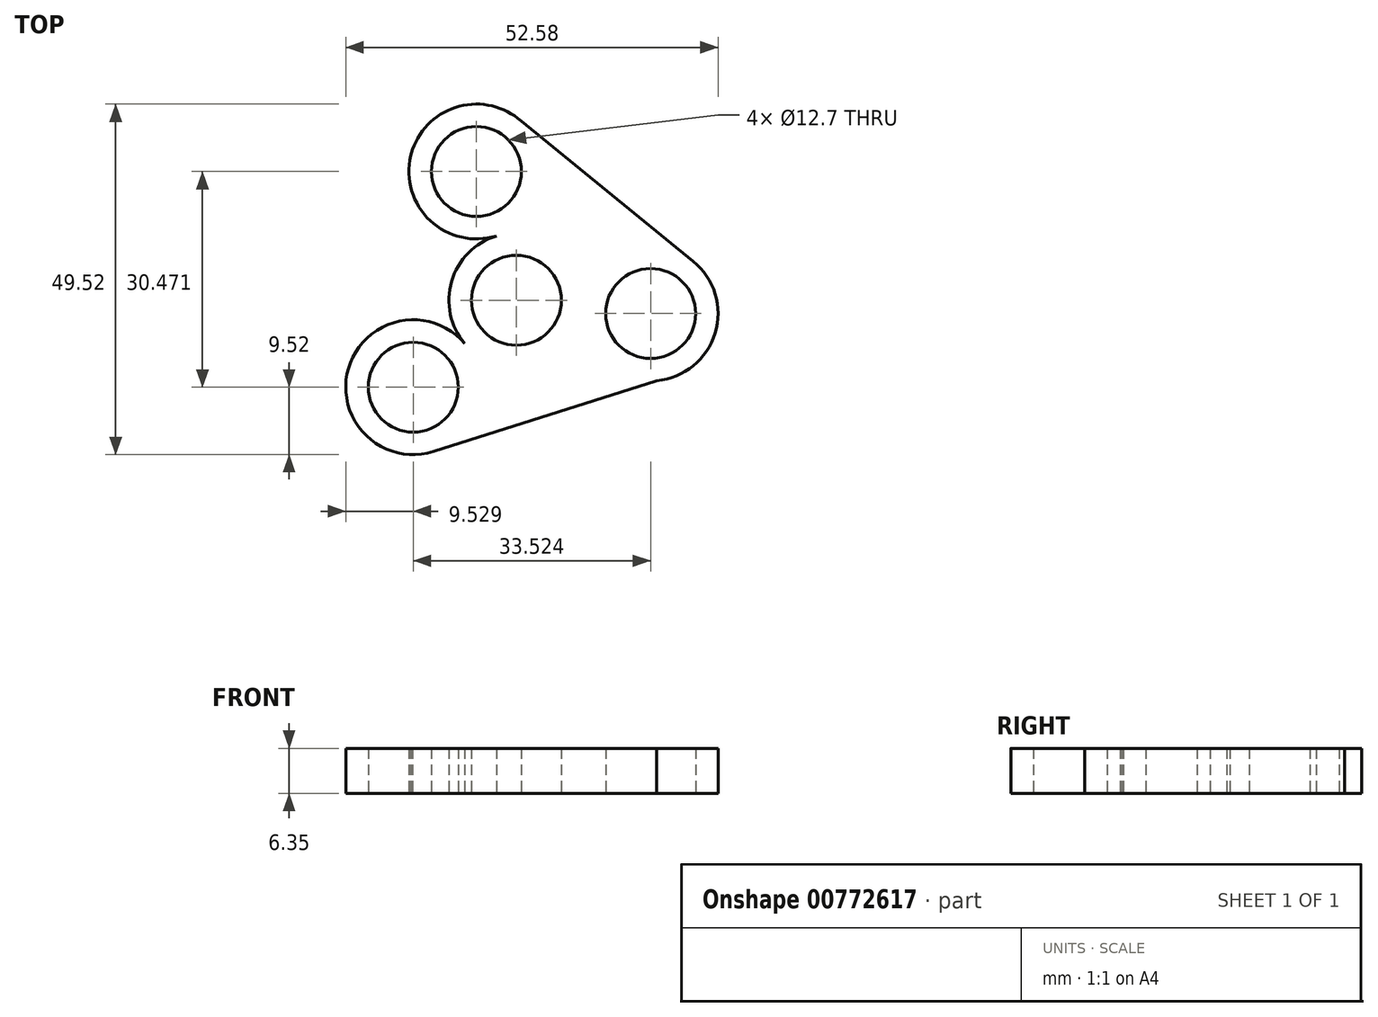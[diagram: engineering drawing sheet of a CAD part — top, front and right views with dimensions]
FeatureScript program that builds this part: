
annotation { "Feature Type Name" : "Feature", "Feature Type Description" : "" }
export const myFeature = defineFeature(function(context is Context, id is Id, definition is map)
    precondition{}
    {
        {
            var Q0;
            Q0=qCreatedBy(makeId("Top.planeOp"),FACE);
            var sketch = newSketch(context, id + "F0", { "sketchPlane" : qUnion([Q0])});
            skCircle(sketch, "E0", {"center": v(-56, 50.78) * mm, "radius": 9.53 * mm});
            skCircle(sketch, "E1", {"center": v(-31.4, 30.71) * mm, "radius": 9.53 * mm});
            skCircle(sketch, "E2", {"center": v(-50.36, 32.59) * mm, "radius": 9.53 * mm});
            skCircle(sketch, "E3", {"center": v(-64.92, 20.31) * mm, "radius": 9.53 * mm});
            skLineSegment(sketch, "E4", {"start": v(-49.69, 57.91) * mm, "end": v(-25.38, 38.1) * mm});
            skLineSegment(sketch, "E5", {"start": v(-30.53, 21.23) * mm, "end": v(-62.04, 11.23) * mm});
            skLineSegment(sketch, "E6", {"start": v(-65, 53.91) * mm, "end": v(-74.06, 22.99) * mm});
            skCircle(sketch, "E7", {"center": v(-64.92, 20.31) * mm, "radius": 6.35 * mm});
            skCircle(sketch, "E8", {"center": v(-50.36, 32.59) * mm, "radius": 6.35 * mm});
            skCircle(sketch, "E9", {"center": v(-56, 50.78) * mm, "radius": 6.35 * mm});
            skCircle(sketch, "E10", {"center": v(-31.4, 30.71) * mm, "radius": 6.35 * mm});
            skSolve(sketch);
        }
        {
            var Q0;
            {var subQ0=sQuery(id+"F0.wireOp",EDGE,"E0");var subQ1=makeQuery(id+"F0.imprint","INTERSECT",VERTEX,{"derivedFrom":[subQ0,sQuery(id+"F0.wireOp",EDGE,"E4")]});Q0=makeQuery(id+"F0.imprint","IMPRINT",FACE,{"disambiguationData":[TD([[makeQuery(id+"F0.imprint","IMPRINT",EDGE,{"disambiguationData":[TD([[subQ1,-1.0]])],"derivedFrom":subQ0}),1.0]])]});}
            var Q1;
            {var subQ0=sQuery(id+"F0.wireOp",EDGE,"E6");var subQ1=sQuery(id+"F0.wireOp",EDGE,"E0");var subQ2=makeQuery(id+"F0.imprint","INTERSECT",VERTEX,{"disambiguationData":[OD(0.0)],"derivedFrom":[subQ1,subQ0]});Q1=makeQuery(id+"F0.imprint","IMPRINT",FACE,{"disambiguationData":[TD([[makeQuery(id+"F0.imprint","IMPRINT",EDGE,{"disambiguationData":[TD([[subQ2,-1.0]])],"derivedFrom":subQ1}),1.0]])]});}
            var Q2;
            {var subQ0=sQuery(id+"F0.wireOp",EDGE,"E1");var subQ1=makeQuery(id+"F0.imprint","INTERSECT",VERTEX,{"derivedFrom":[subQ0,sQuery(id+"F0.wireOp",EDGE,"E4")]});Q2=makeQuery(id+"F0.imprint","IMPRINT",FACE,{"disambiguationData":[TD([[makeQuery(id+"F0.imprint","IMPRINT",EDGE,{"disambiguationData":[TD([[subQ1,-1.0]])],"derivedFrom":subQ0}),1.0]])]});}
            var Q3;
            {var subQ0=sQuery(id+"F0.wireOp",EDGE,"E3");var subQ1=makeQuery(id+"F0.imprint","INTERSECT",VERTEX,{"derivedFrom":[subQ0,sQuery(id+"F0.wireOp",EDGE,"E6")]});Q3=makeQuery(id+"F0.imprint","IMPRINT",FACE,{"disambiguationData":[TD([[makeQuery(id+"F0.imprint","IMPRINT",EDGE,{"disambiguationData":[TD([[subQ1,1.0]])],"derivedFrom":subQ0}),1.0]])]});}
            var Q4;
            {var subQ0=sQuery(id+"F0.wireOp",EDGE,"E6");var subQ1=sQuery(id+"F0.wireOp",EDGE,"E0");var subQ2=makeQuery(id+"F0.imprint","INTERSECT",VERTEX,{"disambiguationData":[OD(1.0)],"derivedFrom":[subQ1,subQ0]});Q4=makeQuery(id+"F0.imprint","IMPRINT",FACE,{"disambiguationData":[TD([[makeQuery(id+"F0.imprint","IMPRINT",EDGE,{"disambiguationData":[TD([[subQ2,-1.0]])],"derivedFrom":subQ1}),-1.0]])]});}
            var Q5;
            {var subQ0=sQuery(id+"F0.wireOp",EDGE,"E4");Q5=makeQuery(id+"F0.imprint","IMPRINT",FACE,{"disambiguationData":[TD([[makeQuery(id+"F0.imprint","IMPRINT",EDGE,{"derivedFrom":subQ0}),-1.0]])]});}
            var Q6;
            {var subQ0=sQuery(id+"F0.wireOp",EDGE,"E5");Q6=makeQuery(id+"F0.imprint","IMPRINT",FACE,{"disambiguationData":[TD([[makeQuery(id+"F0.imprint","IMPRINT",EDGE,{"derivedFrom":subQ0}),-1.0]])]});}
            var Q7;
            {var subQ0=sQuery(id+"F0.wireOp",EDGE,"E2");var subQ1=makeQuery(id+"F0.imprint","INTERSECT",VERTEX,{"derivedFrom":[sQuery(id+"F0.wireOp",EDGE,"E0"),subQ0]});Q7=makeQuery(id+"F0.imprint","IMPRINT",FACE,{"disambiguationData":[TD([[makeQuery(id+"F0.imprint","IMPRINT",EDGE,{"disambiguationData":[TD([[subQ1,-1.0]])],"derivedFrom":subQ0}),1.0]])]});}
            extrude(context, id + "F1", {"entities" : qUnion([Q0, Q1, Q2, Q3, Q4, Q5, Q6, Q7]), "depth" : 6.35 * mm, "offsetDistance" : 25.4 * mm});
        }
    });
